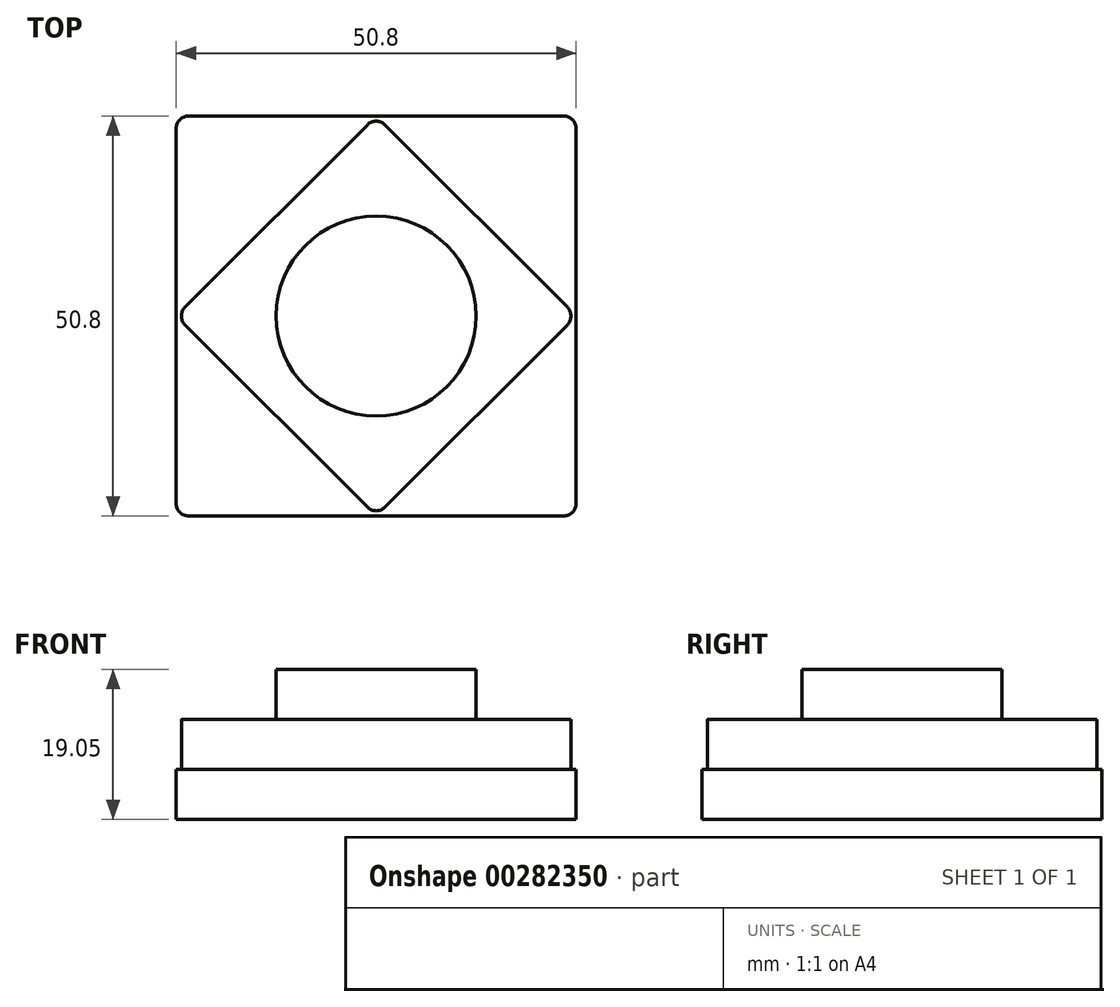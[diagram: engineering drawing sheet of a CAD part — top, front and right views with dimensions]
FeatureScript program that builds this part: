
annotation { "Feature Type Name" : "Feature", "Feature Type Description" : "" }
export const myFeature = defineFeature(function(context is Context, id is Id, definition is map)
    precondition{}
    {
        {
            var Q0;
            Q0=qCreatedBy(makeId("Top.planeOp"),FACE);
            var sketch = newSketch(context, id + "F0", { "sketchPlane" : qUnion([Q0])});
            skLineSegment(sketch, "E0.bottom", {"start": v(25.4, 25.4) * mm, "end": v(-25.4, 25.4) * mm});
            skLineSegment(sketch, "E0.top", {"start": v(25.4, -25.4) * mm, "end": v(-25.4, -25.4) * mm});
            skLineSegment(sketch, "E0.left", {"start": v(25.4, 25.4) * mm, "end": v(25.4, -25.4) * mm});
            skLineSegment(sketch, "E0.right", {"start": v(-25.4, 25.4) * mm, "end": v(-25.4, -25.4) * mm});
            skPoint(sketch, "E0.middle", {"position": v(0, 0) * mm});
            skSolve(sketch);
        }
        {
            var Q0;
            Q0 = qSketchRegion(id + "F0", true);
            extrude(context, id + "F1", {"entities" : qUnion([Q0]), "depth" : 6.35 * mm});
        }
        {
            var Q0;
            Q0=makeQuery(id+"F1.opExtrude","CAP_FACE",FACE,{"disambiguationData":[OSD([sQuery(id+"F0.wireOp",EDGE,"E0.bottom"),sQuery(id+"F0.wireOp",EDGE,"E0.top"),sQuery(id+"F0.wireOp",EDGE,"E0.left"),sQuery(id+"F0.wireOp",EDGE,"E0.right")])],"isStart":false});
            var sketch = newSketch(context, id + "F2", { "sketchPlane" : qUnion([Q0])});
            skLineSegment(sketch, "E1", {"start": v(25.4, 0) * mm, "end": v(0, 25.4) * mm});
            skLineSegment(sketch, "E2", {"start": v(0, 25.4) * mm, "end": v(-25.4, 0) * mm});
            skLineSegment(sketch, "E3", {"start": v(-25.4, 0) * mm, "end": v(0, -25.4) * mm});
            skLineSegment(sketch, "E4", {"start": v(0, -25.4) * mm, "end": v(25.4, 0) * mm});
            skSolve(sketch);
        }
        {
            var Q0;
            Q0 = qSketchRegion(id + "F2", true);
            extrude(context, id + "F3", {"entities" : qUnion([Q0]), "operationType" : NewBodyOperationType.ADD, "depth" : 6.35 * mm});
        }
        {
            var Q0;
            Q0=makeQuery(id+"F3.opExtrude","CAP_FACE",FACE,{"disambiguationData":[OSD([sQuery(id+"F2.wireOp",EDGE,"E1"),sQuery(id+"F2.wireOp",EDGE,"E2"),sQuery(id+"F2.wireOp",EDGE,"E3"),sQuery(id+"F2.wireOp",EDGE,"E4")])],"isStart":false});
            var sketch = newSketch(context, id + "F4", { "sketchPlane" : qUnion([Q0])});
            skCircle(sketch, "E5", {"center": v(0, 0) * mm, "radius": 12.7 * mm});
            skSolve(sketch);
        }
        {
            var Q0;
            Q0 = qSketchRegion(id + "F4", true);
            extrude(context, id + "F5", {"entities" : qUnion([Q0]), "operationType" : NewBodyOperationType.ADD, "depth" : 6.35 * mm});
        }
        {
            var Q0;
            Q0=makeQuery(id+"F3.opExtrude","SWEPT_EDGE",EDGE,{"disambiguationData":[OSD([sQuery(id+"F0.wireOp",EDGE,"E0.right"),sQuery(id+"F2.wireOp",EDGE,"E2"),sQuery(id+"F2.wireOp",EDGE,"E3")])]});
            var Q1;
            Q1=makeQuery(id+"F3.opExtrude","SWEPT_EDGE",EDGE,{"disambiguationData":[OSD([sQuery(id+"F0.wireOp",EDGE,"E0.left"),sQuery(id+"F2.wireOp",EDGE,"E1"),sQuery(id+"F2.wireOp",EDGE,"E4")])]});
            var Q2;
            Q2=makeQuery(id+"F3.opExtrude","SWEPT_EDGE",EDGE,{"disambiguationData":[OSD([sQuery(id+"F0.wireOp",EDGE,"E0.bottom"),sQuery(id+"F2.wireOp",EDGE,"E1"),sQuery(id+"F2.wireOp",EDGE,"E2")])]});
            var Q3;
            Q3=makeQuery(id+"F3.opExtrude","SWEPT_EDGE",EDGE,{"disambiguationData":[OSD([sQuery(id+"F0.wireOp",EDGE,"E0.top"),sQuery(id+"F2.wireOp",EDGE,"E3"),sQuery(id+"F2.wireOp",EDGE,"E4")])]});
            var Q4;
            Q4=makeQuery(id+"F1.opExtrude","SWEPT_EDGE",EDGE,{"disambiguationData":[OSD([sQuery(id+"F0.wireOp",EDGE,"E0.bottom"),sQuery(id+"F0.wireOp",EDGE,"E0.right")])]});
            var Q5;
            Q5=makeQuery(id+"F1.opExtrude","SWEPT_EDGE",EDGE,{"disambiguationData":[OSD([sQuery(id+"F0.wireOp",EDGE,"E0.top"),sQuery(id+"F0.wireOp",EDGE,"E0.right")])]});
            var Q6;
            Q6=makeQuery(id+"F1.opExtrude","SWEPT_EDGE",EDGE,{"disambiguationData":[OSD([sQuery(id+"F0.wireOp",EDGE,"E0.top"),sQuery(id+"F0.wireOp",EDGE,"E0.left")])]});
            var Q7;
            Q7=makeQuery(id+"F1.opExtrude","SWEPT_EDGE",EDGE,{"disambiguationData":[OSD([sQuery(id+"F0.wireOp",EDGE,"E0.bottom"),sQuery(id+"F0.wireOp",EDGE,"E0.left")])]});
            fillet(context, id + "F6", {"entities" : qUnion([Q0, Q1, Q2, Q3, Q4, Q5, Q6, Q7]), "radius" : 1.59 * mm, "tangentPropagation" : true, "allowEdgeOverflow" : false});
        }
    });
